# Revit family: PRE070006-FR
name_source: partatom
category: Appareils sanitaires
revit_build: Autodesk Revit 2017 (Build: 20160225_1515(x64)
units: mm (PartAtom-declared; Revit-internal decimal feet)

## family parameters
Basée sur le plan de construction = Non
Cote de connecteur circulaire = Utiliser le diamètre
Couper avec des vides une fois chargée = Non
Partagée = Non
Point de calcul de pièce = Non
Toujours verticalement = Oui
Type d'élément = Normal

## types (4) — shared parameters
Adresse = 7, RUE RACINE - 92542 MONTROUGE CEDEX FRANCE
Debit = 1.9L/min
Diamètre Nominal = 15 mm  [stored 0.0492126 ft]
Fabricant = LES ROBINETS PRESTO S.A.
Flux = 0.1 L/s
Garantie = 3 ans
Hauteur = 43 mm  [stored 0.141076 ft]
LC = 10 mm  [stored 0.0328084 ft]
Largeur = 43 mm  [stored 0.141076 ft]
Lien CCTP = http://www.prestodatashare.com
Lien fiche produit = http://www.prestodatashare.com
Lien notice d'utilisation = http://www.prestodatashare.com
Matériau = Laiton poli chromé
PC = 25 mm  [stored 0.082021 ft]
Perte de charge = 0.0 Pa
Pression = 1 à 5 bars
Profondeur = 163 mm  [stored 0.534777 ft]
Raccordement = G 1/2'' (15x21) - eau froide ou pre-mixé
URL = http://www.prestodatashare.com
URL Fabricant = http://www.prestodatashare.com
Variantes = 57036 - 57040 - 57044 - 57048

## per-type parameters (varying)
| type | Description | Finition | Fonction | Polantis code | Reference |
| 57040 PRESTO NEO Sensor mural secteur | Robinet electronique mural à détection infrarouge sur plage. Avec cellule optoélectronique, alimentation basse tension  (12-24V AC/DC) dans boîtier externe IP65 étanche (transformateur 230V AC / 12-24V AC non fourni) . Électrovanne externe | Matière et couleur de finition :
- Corps en métal moulé injecté chromé | Débit :
- Jet douchette régulé 1.9l/min
- Aérateur anti-tartre haute qualité
- Dispositif anti-coup de bélier

Alimentation hydraulique :
- G 1/2'' (15x21) - eau froide ou pre-mixé

Alimentation électrique :
- Alimentation électrique basse tension (12-24V AC/DC) dans boîtier externe IP65 étanche (transformateur 230V AC / 12-24V AC non fourni)

Matière et couleur de finition :
- Corps en métal moulé injecté chromé

Résistance thermique :
- Résiste à une température de 75°C durant 30 minutes dans le cadre de chocs thermiques

Sécurité :
- Fermeture automatique de l'électrovanne en cas d'écoulement > à 30s, d'usure de la pile ou de dégradation du détecteur
- Ecoulement automatique de 45 secondes, 24 heures après la dernière utilisation (durée et intervalle réglables)
- Alerte batterie faible (led clignotante)

Livré avec :
- 1 Ecrou de fixation
- 1 Joint et 1 rondelle
- 1 Electrovanne externe
- 1 Alimentation (pile et boitier etanche)
- 1 Joints filtre

Normes / Agréments :
- Laiton conforme aux normes NF EN1982, EN12164, NF EN12165
- Résistant au brouillard salin 200 H (essai NSS) conformément à la norme NF ISO 9227 | PRE07000-a | 57040 |
| 57044 PRESTO NEO Sensor Noir Mat mural pile | Robinet electronique mural à détection infrarouge sur plage. Avec cellule optoélectronique, alimentation par pile lithium 6 V externe. Électrovanne externe | Matière et couleur de finition :
- Corps en métal moulé injecté
- Finition du corps noir mat | Débit :
- Jet douchette régulé 1.9l/min
- Aérateur anti-tartre haute qualité
- Dispositif anti-coup de bélier

Alimentation hydraulique :
- G 1/2'' (15x21) - eau froide ou pre-mixé

Alimentation électrique :
- Pile lithium 6 volts type CRP2 dans boîtier externe IP65 étanche

Matière et couleur de finition :
- Corps en métal moulé injecté
- Finition du corps noir mat

Résistance thermique :
- Résiste à une température de 75°C durant 30 minutes dans le cadre de chocs thermiques

Sécurité :
- Fermeture automatique de l'électrovanne en cas d'écoulement > à 30s, d'usure de la pile ou de dégradation du détecteur
- Ecoulement automatique de 45 secondes, 24 heures après la dernière utilisation (durée et intervalle réglables)
- Alerte batterie faible (led clignotante)

Livré avec :
- 1 Ecrou de fixation
- 1 Joint et 1 rondelle
- 1 Electrovanne externe
- 1 Alimentation (pile et boitier etanche)
- 1 Joints filtre

Normes / Agréments :
- Laiton conforme aux normes NF EN1982, EN12164, NF EN12165
- Résistant au brouillard salin 200 H (essai NSS) conformément à la norme NF ISO 9227 | PRE07000-b | 57044 |
| 57036 PRESTO NEO Sensor mural pile | Robinet electronique mural à détection infrarouge sur plage. Avec cellule optoélectronique, alimentation par pile lithium 6 V externe. Électrovanne externe | Matière et couleur de finition :
- Corps en métal moulé injecté chromé | Débit :
- Jet douchette régulé 1.9l/min
- Aérateur anti-tartre haute qualité
- Dispositif anti-coup de bélier

Alimentation hydraulique :
- G 1/2'' (15x21) - eau froide ou pre-mixé

Alimentation électrique :
- Pile lithium 6 volts type CRP2 dans boîtier externe IP65 étanche

Matière et couleur de finition :
- Corps en métal moulé injecté chromé

Résistance thermique :
- Résiste à une température de 75°C durant 30 minutes dans le cadre de chocs thermiques

Sécurité :
- Fermeture automatique de l'électrovanne en cas d'écoulement > à 30s, d'usure de la pile ou de dégradation du détecteur
- Ecoulement automatique de 45 secondes, 24 heures après la dernière utilisation (durée et intervalle réglables)
- Alerte batterie faible (led clignotante)

Livré avec :
- 1 Ecrou de fixation
- 1 Joint et 1 rondelle
- 1 Electrovanne externe
- 1 Alimentation (pile et boitier etanche)
- 1 Joints filtre

Normes / Agréments :
- Laiton conforme aux normes NF EN1982, EN12164, NF EN12165
- Résistant au brouillard salin 200 H (essai NSS) conformément à la norme NF ISO 9227 | PRE07000- | 57036 |
| 57048 PRESTO NEO Sensor Noir Mat mural secteur | Robinet electronique mural à détection infrarouge sur plage. Avec cellule optoélectronique, alimentation basse tension  (12-24V AC/DC) dans boîtier externe IP65 étanche (transformateur 230V AC / 12-24V AC non fourni) . Électrovanne externe | Matière et couleur de finition :
- Corps en métal moulé injecté
- Finition du corps noir mat | Débit :
- Jet douchette régulé 1.9l/min
- Aérateur anti-tartre haute qualité
- Dispositif anti-coup de bélier

Alimentation hydraulique :
- G 1/2'' (15x21) - eau froide ou pre-mixé

Alimentation électrique :
- Alimentation électrique basse tension (12-24V AC/DC) dans boîtier externe IP65 étanche (transformateur 230V AC / 12-24V AC non fourni)

Matière et couleur de finition :
- Corps en métal moulé injecté
- Finition du corps noir mat
Résistance thermique :
- Résiste à une température de 75°C durant 30 minutes dans le cadre de chocs thermiques

Sécurité :
- Fermeture automatique de l'électrovanne en cas d'écoulement > à 30s, d'usure de la pile ou de dégradation du détecteur
- Ecoulement automatique de 45 secondes, 24 heures après la dernière utilisation (durée et intervalle réglables)
- Alerte batterie faible (led clignotante)

Livré avec :
- 1 Ecrou de fixation
- 1 Joint et 1 rondelle
- 1 Electrovanne externe
- 1 Alimentation (pile et boitier etanche)
- 1 Joints filtre

Normes / Agréments :
- Laiton conforme aux normes NF EN1982, EN12164, NF EN12165
- Résistant au brouillard salin 200 H (essai NSS) conformément à la norme NF ISO 9227 | PRE07000-c | 57048 |

note: column(s) folded — value = type name in every type: Modèle

note: [stored X ft] marks values corroborated as IEEE doubles in the binary element streams (Revit-internal decimal feet)

## geometry (parser evidence)
native form markers: Sweep x2
no freeform markers — native parametric forms only
